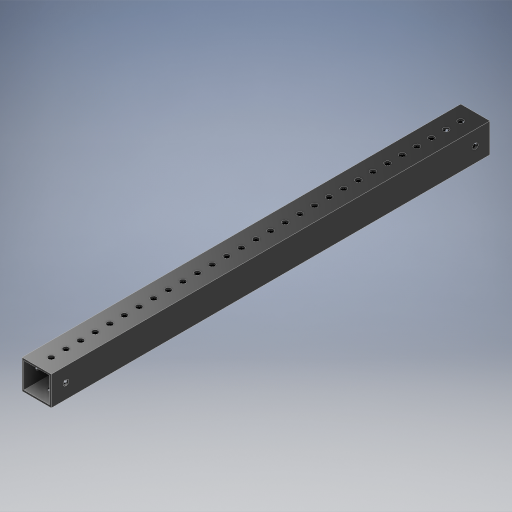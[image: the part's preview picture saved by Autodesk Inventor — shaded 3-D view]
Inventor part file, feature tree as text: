
AUTODESK INVENTOR PART (.ipt)
format: ipt  version: 2024.2 (Build 282272000, 272)  size: 800,256 bytes
history: native  units: in
note: dims shown in document units (in); Inventor stores cm internally (conversion verified against a paired STEP export)
features: other x13, extrude x9, hole x3, pattern_linear x3, mirror x3, sheet_metal_op x1, plane x1
ambient origin geometry x8: Origin, YZ Plane, XZ Plane, XY Plane, X Axis, Y Axis, Z Axis, Center Point
bodies: Solid1 (feature_tree)
feature tree (33):
  other  "Blocks"
  other  "Base Sketch"
  extrude  "Base"  Depth=1.0in
  extrude  "MAX Corner"  Depth=1.0in
  extrude  "MAX Corner Cut"  Depth=0.0625in
  extrude  "Scribe Lines"  Depth=0.0625in
  other  "Side Middle"
  other  "Top Middle"
  other  "Side Holes Sketch"
  hole  "Top Side Hole"  [1 undecoded]
  hole  "Mid Side Hole"  [1 undecoded]
  hole  "Btm Side Hole"  [1 undecoded]
  pattern_linear  "Side Holes"  Spacing1=0.04in  [1 undecoded]
  mirror  "Side Mirror"
  extrude  "MAXTube Hole"  Depth=0.04in
  extrude  "MAXTube Outside"  Depth=15.0in
  pattern_linear  "MAXTube Pattern"  Spacing1=0.0in  [1 undecoded]
  mirror  "MAXTube Mirror"
  extrude  "Left Top Hole"  Depth=15.0in
  extrude  "Mid Top Hole"  TaperAngle=0.0deg  [1 undecoded]
  extrude  "Right Top Hole"  TaperAngle=0.0deg  [1 undecoded]
  pattern_linear  "Top Holes"  Spacing1=0.005in  [1 undecoded]
  mirror  "Top Mirror"
  sheet_metal_op  "Corner"
  other  "MAXTube"
  plane  "Work Plane3"
  other  "Corner:5"
  other  "Corner:6"
  other  "Corner:7"
  other  "Corner:8"
  other  "MAXTube:1"
  other  "MAXTube:2"
  other  "MAXTube:3"
note: 8 required parameter values undecoded (feature->parameter linkage not recoverable at this tier; creation-order binding heuristic only, values carry confidence <= 0.55)
